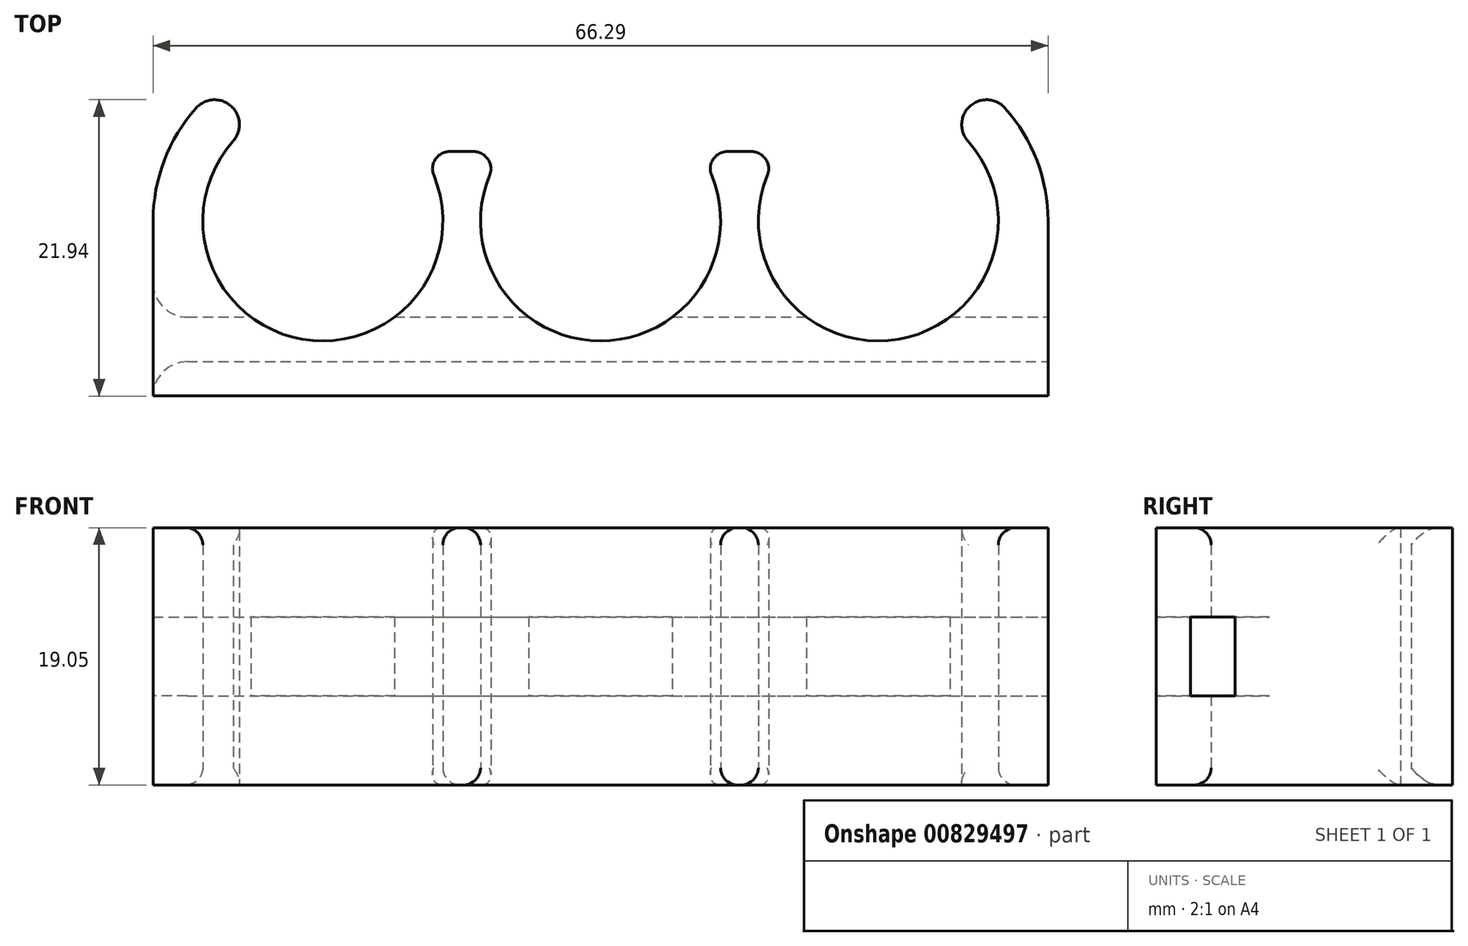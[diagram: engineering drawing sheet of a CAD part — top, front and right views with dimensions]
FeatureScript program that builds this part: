
annotation { "Feature Type Name" : "Feature", "Feature Type Description" : "" }
export const myFeature = defineFeature(function(context is Context, id is Id, definition is map)
    precondition{}
    {
        {
            var Q0;
            Q0=qCreatedBy(makeId("Top.planeOp"),FACE);
            var sketch = newSketch(context, id + "F0", { "sketchPlane" : qUnion([Q0])});
            skLineSegment(sketch, "E0.direction1", {"start": v(0, 0) * mm, "end": v(20.57, 0) * mm, "construction": true});
            skLineSegment(sketch, "E1", {"start": v(53.72, -12.97) * mm, "end": v(53.72, 0) * mm});
            skLineSegment(sketch, "E2", {"start": v(9.4, 5.14) * mm, "end": v(11.18, 5.14) * mm});
            skLineSegment(sketch, "E3", {"start": v(29.97, 5.14) * mm, "end": v(31.75, 5.14) * mm});
            skArc(sketch, "E4", {"start": v(53.72, 0) * mm, "mid": v(52.9, 4.47) * mm, "end": v(50.54, 8.35) * mm});
            skArc(sketch, "E5", {"start": v(50.54, 8.35) * mm, "mid": v(47.94, 8.5) * mm, "end": v(47.79, 5.9) * mm});
            skLineSegment(sketch, "E6", {"start": v(20.57, 0) * mm, "end": v(20.57, 18.34) * mm});
            skArc(sketch, "E7.MirrorCS", {"start": v(-9.4, 8.35) * mm, "mid": v(-6.8, 8.5) * mm, "end": v(-6.64, 5.9) * mm});
            skArc(sketch, "E8.MirrorCS", {"start": v(-12.57, 0) * mm, "mid": v(-11.75, 4.47) * mm, "end": v(-9.4, 8.35) * mm});
            skLineSegment(sketch, "E9.MirrorCS", {"start": v(-12.57, -12.97) * mm, "end": v(-12.57, 0) * mm});
            skLineSegment(sketch, "E10", {"start": v(-12.57, -12.97) * mm, "end": v(53.72, -12.97) * mm});
            skArc(sketch, "E11", {"start": v(8.22, 3.38) * mm, "mid": v(-1.5, -8.76) * mm, "end": v(-6.63, 5.93) * mm});
            skArc(sketch, "E12", {"start": v(28.8, 3.38) * mm, "mid": v(20.57, -8.89) * mm, "end": v(12.35, 3.38) * mm});
            skArc(sketch, "E13", {"start": v(47.79, 5.9) * mm, "mid": v(42.64, -8.76) * mm, "end": v(32.93, 3.38) * mm});
            skPoint(sketch, "E14.visualSharp", {"position": v(7.26, 5.14) * mm});
            skArc(sketch, "E14.filletArc", {"start": v(9.4, 5.14) * mm, "mid": v(8.34, 4.57) * mm, "end": v(8.22, 3.38) * mm});
            skPoint(sketch, "E15.visualSharp", {"position": v(13.32, 5.14) * mm});
            skArc(sketch, "E15.filletArc", {"start": v(12.35, 3.38) * mm, "mid": v(12.23, 4.57) * mm, "end": v(11.18, 5.14) * mm});
            skPoint(sketch, "E16.visualSharp", {"position": v(27.83, 5.14) * mm});
            skArc(sketch, "E16.filletArc", {"start": v(29.97, 5.14) * mm, "mid": v(28.91, 4.57) * mm, "end": v(28.8, 3.38) * mm});
            skPoint(sketch, "E17.visualSharp", {"position": v(33.9, 5.14) * mm});
            skArc(sketch, "E17.filletArc", {"start": v(32.93, 3.38) * mm, "mid": v(32.8, 4.57) * mm, "end": v(31.75, 5.14) * mm});
            skSolve(sketch);
        }
        {
            var Q0;
            Q0=makeQuery(id+"F0.imprint","IMPRINT",FACE,{"disambiguationData":[TD([[makeQuery(id+"F0.imprint","IMPRINT",EDGE,{"derivedFrom":sQuery(id+"F0.wireOp",EDGE,"E1")}),1.0]])]});
            extrude(context, id + "F1", {"entities" : qUnion([Q0]), "depth" : 19.05 * mm, "offsetDistance" : 25.4 * mm});
        }
        {
            var Q0;
            Q0=makeQuery(id+"F1.opExtrude","SWEPT_FACE",FACE,{"disambiguationData":[OSD([sQuery(id+"F0.wireOp",EDGE,"E1")])]});
            cPlane(context, id + "F2", {"entities" : qUnion([Q0]), "cplaneType" : CPlaneType.OFFSET, "offset" : 0 * mm, "width" : 152.4 * mm, "height" : 152.4 * mm});
        }
        {
            var Q0;
            Q0=qCreatedBy(id+"F2.planeOp",FACE);
            var sketch = newSketch(context, id + "F3", { "sketchPlane" : qUnion([Q0])});
            skLineSegment(sketch, "E18.bottom", {"start": v(-10.43, 12.45) * mm, "end": v(-7.13, 12.45) * mm});
            skLineSegment(sketch, "E18.top", {"start": v(-10.43, 6.6) * mm, "end": v(-7.13, 6.6) * mm});
            skLineSegment(sketch, "E18.left", {"start": v(-10.43, 12.45) * mm, "end": v(-10.43, 6.6) * mm});
            skLineSegment(sketch, "E18.right", {"start": v(-7.13, 12.45) * mm, "end": v(-7.13, 6.6) * mm});
            skLineSegment(sketch, "E19", {"start": v(-7.13, 9.53) * mm, "end": v(-10.43, 9.53) * mm, "construction": true});
            skLineSegment(sketch, "E20", {"start": v(-10.43, 9.53) * mm, "end": v(-12.97, 9.53) * mm, "construction": true});
            skSolve(sketch);
        }
        {
            var Q0;
            Q0=makeQuery(id+"F3.imprint","IMPRINT",FACE,{"disambiguationData":[TD([[makeQuery(id+"F3.imprint","IMPRINT",EDGE,{"derivedFrom":sQuery(id+"F3.wireOp",EDGE,"E18.bottom")}),-1.0]])]});
            extrude(context, id + "F4", {"entities" : qUnion([Q0]), "operationType" : NewBodyOperationType.REMOVE, "endBound" : BoundingType.THROUGH_ALL, "oppositeDirection" : true, "depth" : 25.4 * mm, "offsetDistance" : 25.4 * mm});
        }
        {
            var Q0;
            Q0=makeQuery(id+"F4.boolean.opBoolean","COPY",EDGE,{"derivedFrom":makeQuery(id+"F4.opExtrude","CAP_EDGE",EDGE,{"disambiguationData":[OSD([sQuery(id+"F3.wireOp",EDGE,"E18.left")])],"isStart":true})});
            var Q1;
            Q1=makeQuery(id+"F4.boolean.opBoolean","COPY",EDGE,{"derivedFrom":makeQuery(id+"F4.opExtrude","CAP_EDGE",EDGE,{"disambiguationData":[OSD([sQuery(id+"F3.wireOp",EDGE,"E18.right")])],"isStart":true})});
            var Q2;
            Q2=makeQuery(id+"F4.boolean.opBoolean","INTERSECT",EDGE,{"derivedFrom":[makeQuery(id+"F1.opExtrude","SWEPT_FACE",FACE,{"disambiguationData":[OSD([sQuery(id+"F0.wireOp",EDGE,"E9.MirrorCS")])]}),makeQuery(id+"F4.opExtrude","SWEPT_FACE",FACE,{"disambiguationData":[OSD([sQuery(id+"F3.wireOp",EDGE,"E18.right")])]})]});
            var Q3;
            Q3=makeQuery(id+"F4.boolean.opBoolean","INTERSECT",EDGE,{"derivedFrom":[makeQuery(id+"F1.opExtrude","SWEPT_FACE",FACE,{"disambiguationData":[OSD([sQuery(id+"F0.wireOp",EDGE,"E9.MirrorCS")])]}),makeQuery(id+"F4.opExtrude","SWEPT_FACE",FACE,{"disambiguationData":[OSD([sQuery(id+"F3.wireOp",EDGE,"E18.left")])]})]});
            fillet(context, id + "F5", {"entities" : qUnion([Q0, Q1, Q2, Q3]), "radius" : 2.54 * mm, "tangentPropagation" : true, "allowEdgeOverflow" : false});
        }
        {
            var Q0;
            Q0=makeQuery(id+"F1.opExtrude","CAP_EDGE",EDGE,{"disambiguationData":[OSD([sQuery(id+"F0.wireOp",EDGE,"E13")])],"isStart":true});
            var Q1;
            Q1=makeQuery(id+"F1.opExtrude","CAP_EDGE",EDGE,{"disambiguationData":[OSD([sQuery(id+"F0.wireOp",EDGE,"E12")])],"isStart":true});
            var Q2;
            Q2=makeQuery(id+"F1.opExtrude","CAP_EDGE",EDGE,{"disambiguationData":[OSD([sQuery(id+"F0.wireOp",EDGE,"E11")])],"isStart":true});
            var Q3;
            Q3=makeQuery(id+"F1.opExtrude","CAP_EDGE",EDGE,{"disambiguationData":[OSD([sQuery(id+"F0.wireOp",EDGE,"E11")])],"isStart":false});
            var Q4;
            Q4=makeQuery(id+"F1.opExtrude","CAP_EDGE",EDGE,{"disambiguationData":[OSD([sQuery(id+"F0.wireOp",EDGE,"E12")])],"isStart":false});
            var Q5;
            Q5=makeQuery(id+"F1.opExtrude","CAP_EDGE",EDGE,{"disambiguationData":[OSD([sQuery(id+"F0.wireOp",EDGE,"E13")])],"isStart":false});
            fillet(context, id + "F6", {"entities" : qUnion([Q0, Q1, Q2, Q3, Q4, Q5]), "radius" : 1.27 * mm, "allowEdgeOverflow" : false});
        }
    });
